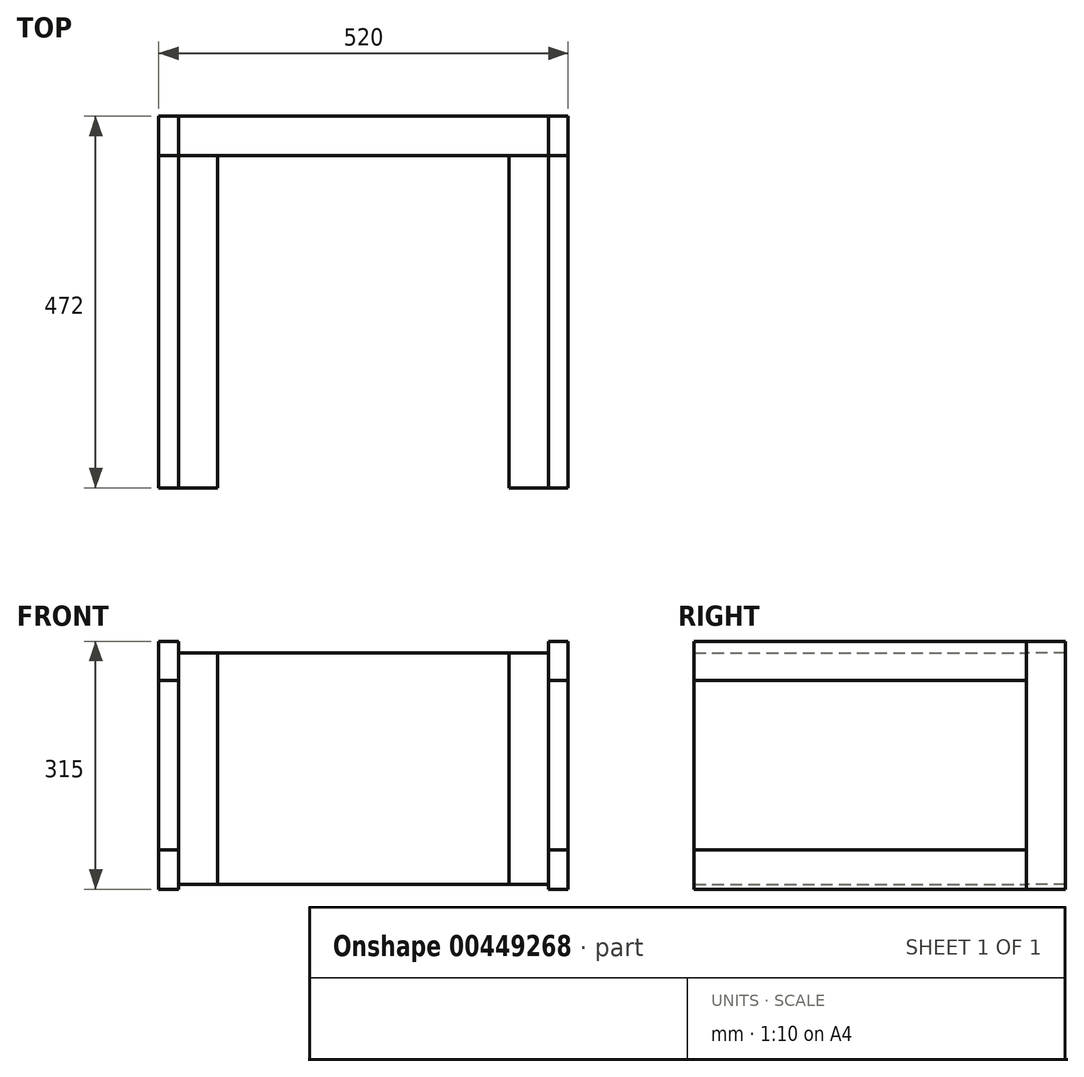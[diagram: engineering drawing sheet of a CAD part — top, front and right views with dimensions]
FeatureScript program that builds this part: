
annotation { "Feature Type Name" : "Feature", "Feature Type Description" : "" }
export const myFeature = defineFeature(function(context is Context, id is Id, definition is map)
    precondition{}
    {
        {
            assignVariable(context, id + "F0", {"variableType" : VariableType.LENGTH, "name" : "W50", "lengthValue" : 50 * mm});
        }
        {
            var Q0;
            Q0=qCreatedBy(makeId("Front.planeOp"),FACE);
            var sketch = newSketch(context, id + "F1", { "sketchPlane" : qUnion([Q0])});
            skLineSegment(sketch, "E0.bottom", {"start": v(-256.25, -149.43) * mm, "end": v(113.75, -149.43) * mm});
            skLineSegment(sketch, "E0.top", {"start": v(-256.25, 144.57) * mm, "end": v(113.75, 144.57) * mm});
            skLineSegment(sketch, "E0.left", {"start": v(-256.25, -149.43) * mm, "end": v(-256.25, 144.57) * mm});
            skLineSegment(sketch, "E0.right", {"start": v(113.75, -149.43) * mm, "end": v(113.75, 144.57) * mm});
            skLineSegment(sketch, "E1.bottom", {"start": v(113.75, -149.43) * mm, "end": v(113.75, -149.43) * mm});
            skLineSegment(sketch, "E1.top", {"start": v(113.75, 144.57) * mm, "end": v(113.75, 144.57) * mm});
            skLineSegment(sketch, "E2.bottom", {"start": v(113.75, -149.43) * mm, "end": v(163.75, -149.43) * mm});
            skLineSegment(sketch, "E2.top", {"start": v(113.75, 144.57) * mm, "end": v(163.75, 144.57) * mm});
            skLineSegment(sketch, "E2.right", {"start": v(163.75, -149.43) * mm, "end": v(163.75, 144.57) * mm});
            skLineSegment(sketch, "E3.bottom", {"start": v(-256.25, -149.43) * mm, "end": v(-306.25, -149.43) * mm});
            skLineSegment(sketch, "E3.top", {"start": v(-256.25, 144.57) * mm, "end": v(-306.25, 144.57) * mm});
            skLineSegment(sketch, "E3.right", {"start": v(-306.25, -149.43) * mm, "end": v(-306.25, 144.57) * mm});
            skLineSegment(sketch, "E4.bottom", {"start": v(-306.25, 144.57) * mm, "end": v(163.75, 144.57) * mm});
            skLineSegment(sketch, "E4.top", {"start": v(-306.25, 159.57) * mm, "end": v(163.75, 159.57) * mm});
            skLineSegment(sketch, "E4.left", {"start": v(-306.25, 144.57) * mm, "end": v(-306.25, 159.57) * mm});
            skLineSegment(sketch, "E4.right", {"start": v(163.75, 144.57) * mm, "end": v(163.75, 159.57) * mm});
            skLineSegment(sketch, "E5.bottom", {"start": v(-306.25, 159.57) * mm, "end": v(-331.25, 159.57) * mm});
            skLineSegment(sketch, "E5.top", {"start": v(-306.25, 109.57) * mm, "end": v(-331.25, 109.57) * mm});
            skLineSegment(sketch, "E5.left", {"start": v(-306.25, 159.57) * mm, "end": v(-306.25, 109.57) * mm});
            skLineSegment(sketch, "E5.right", {"start": v(-331.25, 159.57) * mm, "end": v(-331.25, 109.57) * mm});
            skLineSegment(sketch, "E6.bottom", {"start": v(163.75, 159.57) * mm, "end": v(188.75, 159.57) * mm});
            skLineSegment(sketch, "E6.top", {"start": v(163.75, 109.57) * mm, "end": v(188.75, 109.57) * mm});
            skLineSegment(sketch, "E6.left", {"start": v(163.75, 159.57) * mm, "end": v(163.75, 109.57) * mm});
            skLineSegment(sketch, "E6.right", {"start": v(188.75, 159.57) * mm, "end": v(188.75, 109.57) * mm});
            skLineSegment(sketch, "E7.top", {"start": v(-331.25, 159.57) * mm, "end": v(188.75, 159.57) * mm});
            skLineSegment(sketch, "E8.bottom", {"start": v(-306.25, -149.43) * mm, "end": v(163.75, -149.43) * mm});
            skLineSegment(sketch, "E8.top", {"start": v(-306.25, -155.43) * mm, "end": v(163.75, -155.43) * mm});
            skLineSegment(sketch, "E8.left", {"start": v(-306.25, -149.43) * mm, "end": v(-306.25, -155.43) * mm});
            skLineSegment(sketch, "E8.right", {"start": v(163.75, -149.43) * mm, "end": v(163.75, -155.43) * mm});
            skLineSegment(sketch, "E9.bottom", {"start": v(-306.25, -155.43) * mm, "end": v(-331.25, -155.43) * mm});
            skLineSegment(sketch, "E9.top", {"start": v(-306.25, -105.43) * mm, "end": v(-331.25, -105.43) * mm});
            skLineSegment(sketch, "E9.left", {"start": v(-306.25, -155.43) * mm, "end": v(-306.25, -105.43) * mm});
            skLineSegment(sketch, "E9.right", {"start": v(-331.25, -155.43) * mm, "end": v(-331.25, -105.43) * mm});
            skLineSegment(sketch, "E10.bottom", {"start": v(163.75, -155.43) * mm, "end": v(188.75, -155.43) * mm});
            skLineSegment(sketch, "E10.top", {"start": v(163.75, -105.43) * mm, "end": v(188.75, -105.43) * mm});
            skLineSegment(sketch, "E10.left", {"start": v(163.75, -155.43) * mm, "end": v(163.75, -105.43) * mm});
            skLineSegment(sketch, "E10.right", {"start": v(188.75, -155.43) * mm, "end": v(188.75, -105.43) * mm});
            skLineSegment(sketch, "E11.top", {"start": v(-331.25, -155.43) * mm, "end": v(188.75, -155.43) * mm});
            skLineSegment(sketch, "E11.left", {"start": v(-331.25, 159.57) * mm, "end": v(-331.25, -155.43) * mm});
            skLineSegment(sketch, "E11.right", {"start": v(188.75, 159.57) * mm, "end": v(188.75, -155.43) * mm});
            skSolve(sketch);
        }
        {
            var Q0;
            {var subQ1=sQuery(id+"F1.wireOp",EDGE,"E5.top");Q0=makeQuery(id+"F1.imprint","IMPRINT",FACE,{"disambiguationData":[TD([[makeQuery(id+"F1.imprint","IMPRINT",EDGE,{"derivedFrom":subQ1}),-1.0]])]});}
            var Q1;
            {var subQ0=sQuery(id+"F1.wireOp",EDGE,"BOletkua-dOb9-VhyX-SVnv-GYsZEf0WnTnK.top");Q1=makeQuery(id+"F1.imprint","IMPRINT",FACE,{"disambiguationData":[TD([[makeQuery(id+"F1.imprint","IMPRINT",EDGE,{"derivedFrom":subQ0}),1.0]])]});}
            var Q2;
            {var subQ0=sQuery(id+"F1.wireOp",EDGE,"e7XpCmME-m576-QVir-dCnz-8zK2rwa17JC3.top");Q2=makeQuery(id+"F1.imprint","IMPRINT",FACE,{"disambiguationData":[TD([[makeQuery(id+"F1.imprint","IMPRINT",EDGE,{"derivedFrom":subQ0}),-1.0]])]});}
            var Q3;
            {var subQ5=sQuery(id+"F1.wireOp",EDGE,"E6.top");Q3=makeQuery(id+"F1.imprint","IMPRINT",FACE,{"disambiguationData":[TD([[makeQuery(id+"F1.imprint","IMPRINT",EDGE,{"derivedFrom":subQ5}),1.0]])]});}
            extrude(context, id + "F2", {"entities" : qUnion([Q0, Q1, Q2, Q3]), "depth" : 422 * mm, "offsetDistance" : 25 * mm});
        }
        {
            var Q0;
            {var subQ4=sQuery(id+"F1.wireOp",EDGE,"E0.left");Q0=makeQuery(id+"F1.imprint","IMPRINT",FACE,{"disambiguationData":[TD([[makeQuery(id+"F1.imprint","IMPRINT",EDGE,{"derivedFrom":subQ4}),1.0]])]});}
            var Q1;
            {var subQ4=sQuery(id+"F1.wireOp",EDGE,"E0.right");Q1=makeQuery(id+"F1.imprint","IMPRINT",FACE,{"disambiguationData":[TD([[makeQuery(id+"F1.imprint","IMPRINT",EDGE,{"derivedFrom":subQ4}),-1.0]])]});}
            extrude(context, id + "F3", {"entities" : qUnion([Q0, Q1]), "depth" : 422 * mm, "offsetDistance" : 25 * mm});
        }
        {
            var Q0;
            {var subQ5=sQuery(id+"F1.wireOp",EDGE,"E9.top");Q0=makeQuery(id+"F1.imprint","IMPRINT",FACE,{"disambiguationData":[TD([[makeQuery(id+"F1.imprint","IMPRINT",EDGE,{"derivedFrom":subQ5}),1.0]])]});}
            var Q1;
            {var subQ5=sQuery(id+"F1.wireOp",EDGE,"E10.top");Q1=makeQuery(id+"F1.imprint","IMPRINT",FACE,{"disambiguationData":[TD([[makeQuery(id+"F1.imprint","IMPRINT",EDGE,{"derivedFrom":subQ5}),-1.0]])]});}
            extrude(context, id + "F4", {"entities" : qUnion([Q0, Q1]), "depth" : 422 * mm, "offsetDistance" : 25 * mm});
        }
        {
            var Q0;
            {var subQ1=sQuery(id+"F1.wireOp",EDGE,"E5.top");Q0=makeQuery(id+"F1.imprint","IMPRINT",FACE,{"disambiguationData":[TD([[makeQuery(id+"F1.imprint","IMPRINT",EDGE,{"derivedFrom":subQ1}),-1.0]])]});}
            var Q1;
            Q1=makeQuery(id+"F1.imprint","IMPRINT",FACE,{"disambiguationData":[TD([[makeQuery(id+"F1.imprint","IMPRINT",EDGE,{"derivedFrom":sQuery(id+"F1.wireOp",EDGE,"E3.right")}),1.0]])]});
            var Q2;
            {var subQ5=sQuery(id+"F1.wireOp",EDGE,"E9.top");Q2=makeQuery(id+"F1.imprint","IMPRINT",FACE,{"disambiguationData":[TD([[makeQuery(id+"F1.imprint","IMPRINT",EDGE,{"derivedFrom":subQ5}),1.0]])]});}
            var Q3;
            {var subQ1=sQuery(id+"F1.wireOp",EDGE,"E8.bottom");var subQ9=makeQuery(id+"F1.imprint","INTERSECT",VERTEX,{"derivedFrom":[sQuery(id+"F1.wireOp",EDGE,"E0.left"),subQ1]});Q3=makeQuery(id+"F1.imprint","IMPRINT",FACE,{"disambiguationData":[TD([[makeQuery(id+"F1.imprint","IMPRINT",EDGE,{"disambiguationData":[TD([[subQ9,1.0]])],"derivedFrom":subQ1}),-1.0]])]});}
            var Q4;
            {var subQ4=sQuery(id+"F1.wireOp",EDGE,"E0.left");Q4=makeQuery(id+"F1.imprint","IMPRINT",FACE,{"disambiguationData":[TD([[makeQuery(id+"F1.imprint","IMPRINT",EDGE,{"derivedFrom":subQ4}),1.0]])]});}
            var Q5;
            {var subQ0=sQuery(id+"F1.wireOp",EDGE,"E0.right");Q5=makeQuery(id+"F1.imprint","IMPRINT",FACE,{"disambiguationData":[TD([[makeQuery(id+"F1.imprint","IMPRINT",EDGE,{"derivedFrom":subQ0}),1.0]])]});}
            var Q6;
            {var subQ1=sQuery(id+"F1.wireOp",EDGE,"E4.bottom");var subQ8=makeQuery(id+"F1.imprint","INTERSECT",VERTEX,{"derivedFrom":[sQuery(id+"F1.wireOp",EDGE,"E0.left"),subQ1]});Q6=makeQuery(id+"F1.imprint","IMPRINT",FACE,{"disambiguationData":[TD([[makeQuery(id+"F1.imprint","IMPRINT",EDGE,{"disambiguationData":[TD([[subQ8,1.0]])],"derivedFrom":subQ1}),1.0]])]});}
            var Q7;
            {var subQ4=sQuery(id+"F1.wireOp",EDGE,"E0.right");Q7=makeQuery(id+"F1.imprint","IMPRINT",FACE,{"disambiguationData":[TD([[makeQuery(id+"F1.imprint","IMPRINT",EDGE,{"derivedFrom":subQ4}),-1.0]])]});}
            var Q8;
            {var subQ5=sQuery(id+"F1.wireOp",EDGE,"E6.top");Q8=makeQuery(id+"F1.imprint","IMPRINT",FACE,{"disambiguationData":[TD([[makeQuery(id+"F1.imprint","IMPRINT",EDGE,{"derivedFrom":subQ5}),1.0]])]});}
            var Q9;
            Q9=makeQuery(id+"F1.imprint","IMPRINT",FACE,{"disambiguationData":[TD([[makeQuery(id+"F1.imprint","IMPRINT",EDGE,{"derivedFrom":sQuery(id+"F1.wireOp",EDGE,"E2.right")}),-1.0]])]});
            var Q10;
            {var subQ5=sQuery(id+"F1.wireOp",EDGE,"E10.top");Q10=makeQuery(id+"F1.imprint","IMPRINT",FACE,{"disambiguationData":[TD([[makeQuery(id+"F1.imprint","IMPRINT",EDGE,{"derivedFrom":subQ5}),-1.0]])]});}
            extrude(context, id + "F5", {"entities" : qUnion([Q0, Q1, Q2, Q3, Q4, Q5, Q6, Q7, Q8, Q9, Q10]), "oppositeDirection" : true, "depth" : getVariable(context, 'W50'), "offsetDistance" : 25 * mm});
        }
    });
